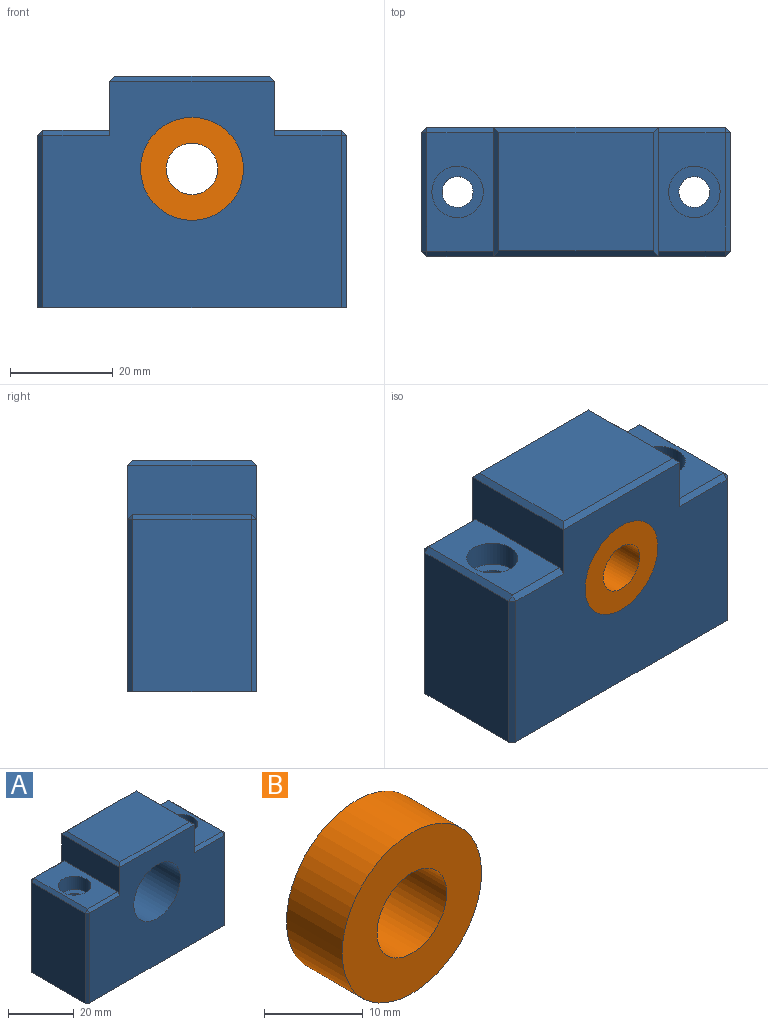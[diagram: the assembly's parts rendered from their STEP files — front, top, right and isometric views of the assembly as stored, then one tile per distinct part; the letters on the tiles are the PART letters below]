
ASSEMBLY  parts=2 mates=1
PART A: 35 faces, bbox 60x25x45 mm
  f0: plane 23x13mm, normal (0,0,1), area 220.5mm2, adj f1,f13,f24,f26,f27
  f1: plane 25x10.5mm, normal (1,0,0), area 238.5mm2, adj f0,f7,f8,f24,f27,f33
  f2: plane 30x23mm, normal (0,0,1), area 690mm2, adj f30,f31,f32,f33
  f3: plane 25x10.5mm, normal (-1,0,0), area 238.5mm2, adj f4,f7,f8,f16,f19,f30
  f4: plane 23x13mm, normal (0,0,1), area 220.5mm2, adj f3,f10,f16,f19,f20
  f5: plane 33.5x23mm, normal (-1,0,0), area 770.5mm2, adj f17,f20,f22,f34
  f6: plane 33.5x23mm, normal (1,0,0), area 770.5mm2, adj f23,f26,f29,f34
  f7: plane 58x44mm, normal (0,1,0), area 1964.8mm2, adj f1,f3,f9,f19,f22,f27,f29,f31
  f8: plane 58x44mm, normal (0,-1,0), area 1964.8mm2, adj f1,f3,f9,f16,f17,f23,f24,f32
  f9: cylinder r=10mm len=25mm, axis (0,-1,0), area 1570.8mm2, adj f7,f8
  f10: cylinder r=5mm len=10mm, axis (0,0,1), area 157.1mm2, adj f4,f11
  f11: plane 10x10mm, normal (0,0,1), area 50.3mm2, adj f10,f12
  f12: cylinder r=3mm len=29.5mm, axis (0,0,1), area 556.1mm2, adj f11,f34
  f13: cylinder r=5mm len=10mm, axis (0,0,1), area 157.1mm2, adj f0,f14
  f14: plane 10x10mm, normal (0,0,1), area 50.3mm2, adj f13,f15
  f15: cylinder r=3mm len=29.5mm, axis (0,0,1), area 556.1mm2, adj f14,f34
  f16: plane 13x1mm, normal (0,-0.71,0.71), area 18.4mm2, adj f3,f4,f8,f18
  f17: plane 33.5x1mm, normal (-0.71,-0.71,0), area 47.4mm2, adj f5,f8,f18,f34
  f18: plane 1x1mm, normal (-0.58,-0.58,0.58), area 0.9mm2, adj f16,f17,f20
  f19: plane 13x1mm, normal (0,0.71,0.71), area 18.4mm2, adj f3,f4,f7,f21
  f20: plane 23x1mm, normal (-0.71,0,0.71), area 32.5mm2, adj f4,f5,f18,f21
  f21: plane 1x1mm, normal (-0.58,0.58,0.58), area 0.9mm2, adj f19,f20,f22
  f22: plane 33.5x1mm, normal (-0.71,0.71,0), area 47.4mm2, adj f5,f7,f21,f34
  f23: plane 33.5x1mm, normal (0.71,-0.71,0), area 47.4mm2, adj f6,f8,f25,f34
  f24: plane 13x1mm, normal (0,-0.71,0.71), area 18.4mm2, adj f0,f1,f8,f25
  f25: plane 1x1mm, normal (0.58,-0.58,0.58), area 0.9mm2, adj f23,f24,f26
  f26: plane 23x1mm, normal (0.71,0,0.71), area 32.5mm2, adj f0,f6,f25,f28
  f27: plane 13x1mm, normal (0,0.71,0.71), area 18.4mm2, adj f0,f1,f7,f28
  f28: plane 1x1mm, normal (0.58,0.58,0.58), area 0.9mm2, adj f26,f27,f29
  f29: plane 33.5x1mm, normal (0.71,0.71,0), area 47.4mm2, adj f6,f7,f28,f34
  f30: plane 25x1mm, normal (-0.71,0,0.71), area 33.9mm2, adj f2,f3,f31,f32
  f31: plane 32x1mm, normal (0,0.71,0.71), area 43.8mm2, adj f2,f7,f30,f33
  f32: plane 32x1mm, normal (0,-0.71,0.71), area 43.8mm2, adj f2,f8,f30,f33
  f33: plane 25x1mm, normal (0.71,0,0.71), area 33.9mm2, adj f1,f2,f31,f32
  f34: plane 60x25mm, normal (0,0,-1), area 1441.5mm2, adj f5,f6,f7,f8,f12,f15,f17,f22
PART B: 4 faces, bbox 20x8x20 mm
  f0: cylinder r=10mm len=20mm, axis (0,1,0), area 502.7mm2, adj f1,f2
  f1: plane 20x20mm, normal (0,-1,0), area 235.6mm2, adj f0,f3
  f2: plane 20x20mm, normal (0,1,0), area 235.6mm2, adj f0,f3
  f3: cylinder r=5mm len=10mm, axis (0,-1,0), area 251.3mm2, adj f1,f2
PLACE A at identity
PLACE B t=(-1.8,8,-5.69)mm
MATE fastened B.f3 <-> A.f9  axis (0,-1,0) through (-1.8,0,-5.69)mm
